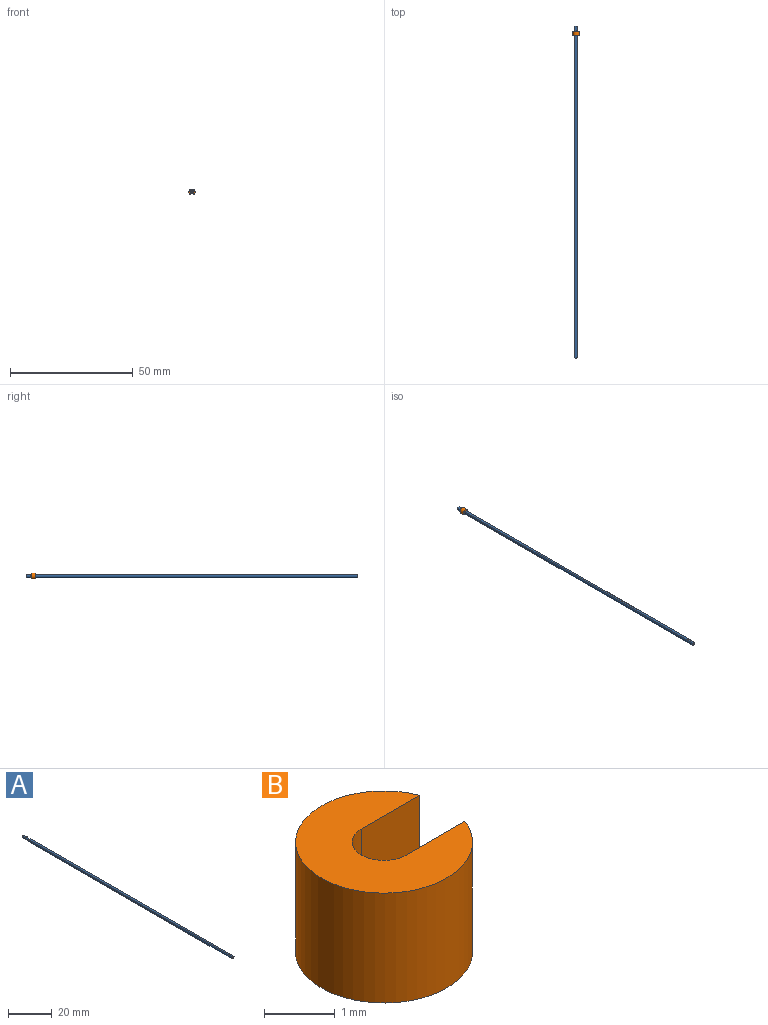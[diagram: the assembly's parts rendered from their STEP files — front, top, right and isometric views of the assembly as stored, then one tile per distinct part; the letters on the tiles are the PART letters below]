
ASSEMBLY  parts=2 mates=1
PART A: 11 faces, bbox 1.5x135x1.3 mm
  f0: plane 1.45x1.28mm, normal (0,1,0), area 1.5mm2, adj f1,f8
  f1: cylinder r=0.72mm len=2mm, axis (0,1,0), area 7.1mm2, adj f0,f2,f8
  f2: plane 1.45x1.28mm, normal (0,-1,0), area 1mm2, adj f1,f3,f8
  f3: cylinder r=0.4mm len=2mm, axis (0,1,0), area 5mm2, adj f2,f4
  f4: plane 1.45x1.28mm, normal (0,1,0), area 1mm2, adj f3,f5,f7
  f5: cylinder r=0.72mm len=131mm, axis (0,1,0), area 462mm2, adj f4,f6,f7
  f6: plane 1.45x1.28mm, normal (0,-1,0), area 0.8mm2, adj f5,f7,f9
  f7: plane 131x0.94mm, normal (0,0,1), area 123.8mm2, adj f4,f5,f6
  f8: plane 2x0.94mm, normal (0,0,1), area 1.9mm2, adj f0,f1,f2
  f9: cylinder r=0.5mm len=3mm, axis (0,-1,0), area 9.4mm2, adj f6,f10
  f10: plane 1x1mm, normal (0,-1,0), area 0.8mm2, adj f9
PART B: 6 faces, bbox 2.4x2.5x1.9 mm
  f0: cylinder r=0.45mm len=1.9mm, axis (0,0,-1), area 2.7mm2, adj f1,f3,f4,f5
  f1: plane 1.9x1.17mm, normal (0,-1,0), area 2.2mm2, adj f0,f2,f4,f5
  f2: cylinder r=1.25mm len=2.5mm, axis (0,0,-1), area 13.2mm2, adj f1,f3,f4,f5
  f3: plane 1.9x1.17mm, normal (0,1,0), area 2.2mm2, adj f0,f2,f4,f5
  f4: plane 2.5x2.42mm, normal (0,0,1), area 3.5mm2, adj f0,f1,f2,f3
  f5: plane 2.5x2.42mm, normal (0,0,-1), area 3.5mm2, adj f0,f1,f2,f3
PLACE A t=(26.74,-54.12,3.65)mm
PLACE B rot(axis=(-0.58,0.58,0.58),120deg) t=(26.74,63.26,3.65)mm
MATE slider A.f1 <-> B.f2  axis (0,1,0) through (26.74,63.2,3.65)mm
